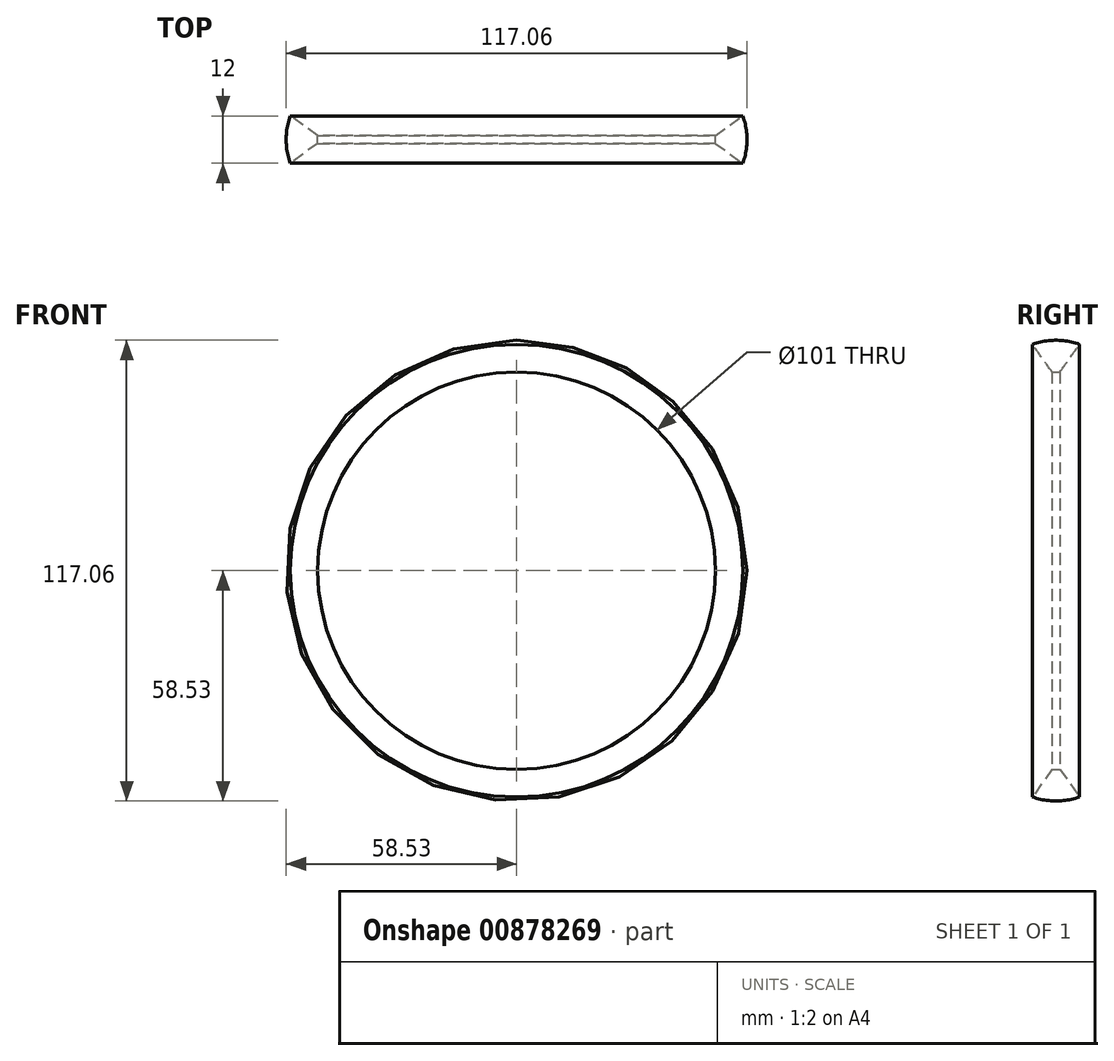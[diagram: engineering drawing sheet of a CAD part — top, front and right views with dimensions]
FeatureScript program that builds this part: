
annotation { "Feature Type Name" : "Feature", "Feature Type Description" : "" }
export const myFeature = defineFeature(function(context is Context, id is Id, definition is map)
    precondition{}
    {
        {
            var Q0;
            Q0=qCreatedBy(makeId("Front.planeOp"),FACE);
            var sketch = newSketch(context, id + "F0", { "sketchPlane" : qUnion([Q0])});
            skCircle(sketch, "E0", {"center": v(0, 0) * mm, "radius": 54 * mm});
            skSolve(sketch);
        }
        {
            var Q0;
            Q0=qCreatedBy(makeId("Right.planeOp"),FACE);
            var sketch = newSketch(context, id + "F1", { "sketchPlane" : qUnion([Q0])});
            skLineSegment(sketch, "E1.bottom", {"start": v(6, 50.5) * mm, "end": v(-6, 50.5) * mm});
            skLineSegment(sketch, "E1.top", {"start": v(6, 57.5) * mm, "end": v(-6, 57.5) * mm});
            skLineSegment(sketch, "E1.left", {"start": v(6, 50.5) * mm, "end": v(6, 57.5) * mm});
            skLineSegment(sketch, "E1.right", {"start": v(-6, 50.5) * mm, "end": v(-6, 57.5) * mm});
            skPoint(sketch, "E1.middle", {"position": v(0, 54) * mm});
            skLineSegment(sketch, "E2", {"start": v(-6, 57.5) * mm, "end": v(-1, 50.5) * mm});
            skLineSegment(sketch, "E3", {"start": v(6, 57.5) * mm, "end": v(1, 50.5) * mm});
            skArc(sketch, "E4", {"start": v(6, 57.5) * mm, "mid": v(0, 58.53) * mm, "end": v(-6, 57.5) * mm});
            skArc(sketch, "E5", {"start": v(-1, 50.5) * mm, "mid": v(0, 49.99) * mm, "end": v(1, 50.5) * mm});
            skSolve(sketch);
        }
        {
            var Q0;
            Q0=makeQuery(id+"F1.imprint","IMPRINT",FACE,{"disambiguationData":[TD([[makeQuery(id+"F1.imprint","IMPRINT",EDGE,{"derivedFrom":sQuery(id+"F1.wireOp",EDGE,"E1.top")}),1.0]])]});
            var Q1;
            Q1=makeQuery(id+"F1.imprint","IMPRINT",FACE,{"disambiguationData":[TD([[makeQuery(id+"F1.imprint","IMPRINT",EDGE,{"derivedFrom":sQuery(id+"F1.wireOp",EDGE,"E1.top")}),-1.0]])]});
            var Q2;
            Q2=sQuery(id+"F0.wireOp",EDGE,"E0");
            revolve(context, id + "F2", {"surfaceOperationType" : NewSurfaceOperationType.NEW, "entities" : qUnion([Q0, Q1]), "axis" : qUnion([Q2]), "revolveType" : RevolveType.FULL});
        }
    });
